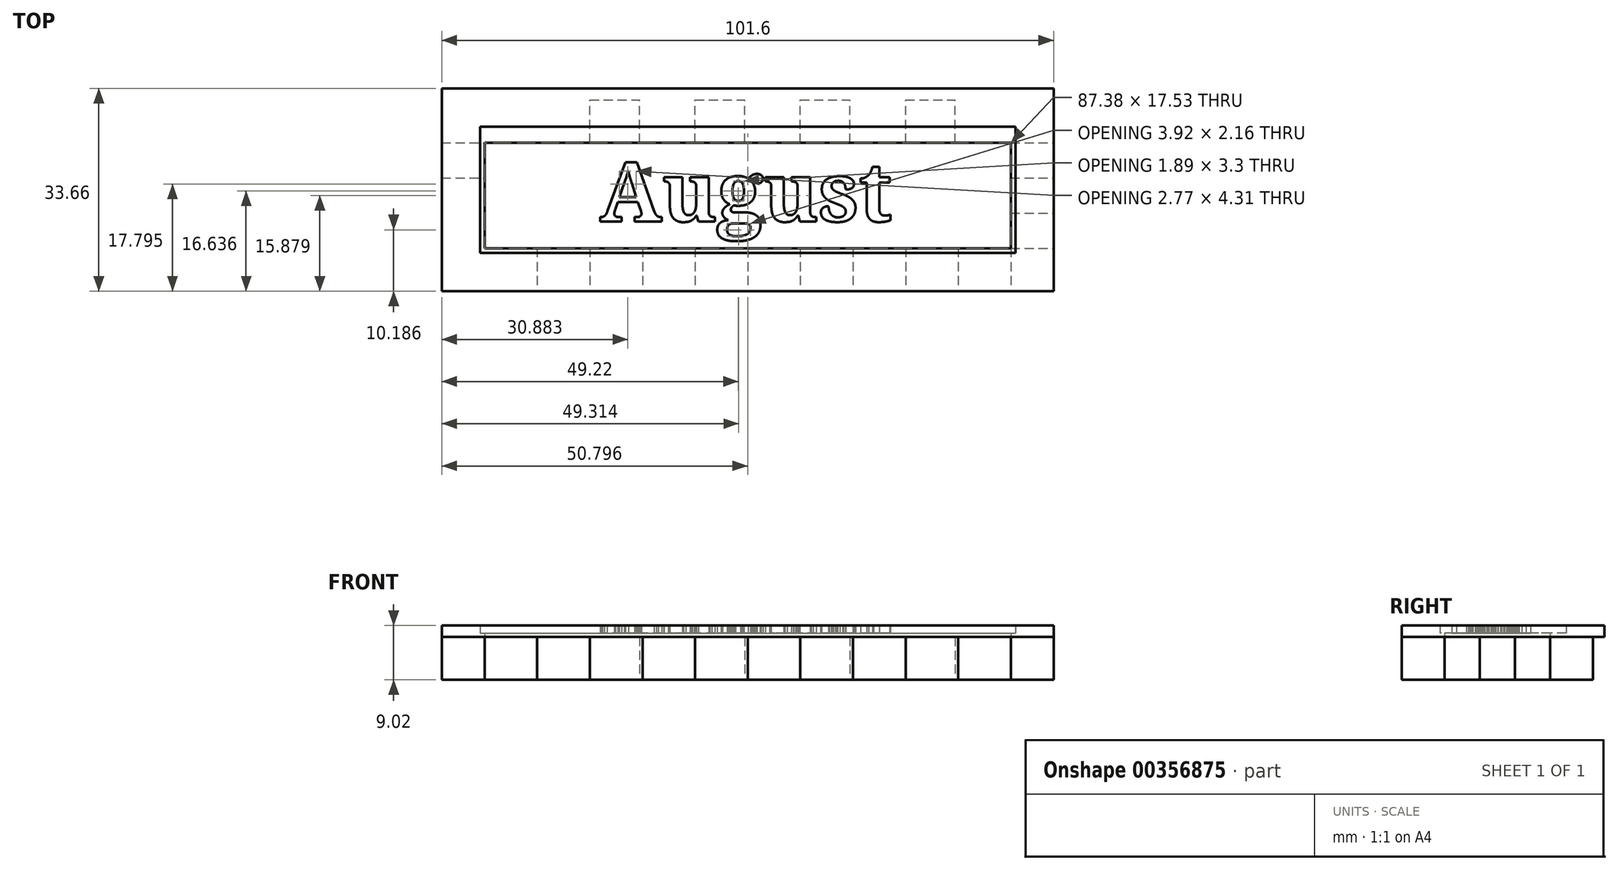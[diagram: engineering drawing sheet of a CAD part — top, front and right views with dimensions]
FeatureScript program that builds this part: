
annotation { "Feature Type Name" : "Feature", "Feature Type Description" : "" }
export const myFeature = defineFeature(function(context is Context, id is Id, definition is map)
    precondition{}
    {
        {
            var Q0;
            Q0=qCreatedBy(makeId("Top.planeOp"),FACE);
            var sketch = newSketch(context, id + "F0", { "sketchPlane" : qUnion([Q0])});
            skLineSegment(sketch, "E0.bottom", {"start": v(-52.12, 11.37) * mm, "end": v(49.48, 11.37) * mm});
            skLineSegment(sketch, "E0.top", {"start": v(-52.12, -20.38) * mm, "end": v(49.48, -20.38) * mm});
            skLineSegment(sketch, "E0.left", {"start": v(-52.12, 11.37) * mm, "end": v(-52.12, -20.38) * mm});
            skLineSegment(sketch, "E0.right", {"start": v(49.48, 11.37) * mm, "end": v(49.48, -20.38) * mm});
            skLineSegment(sketch, "E1.bottom", {"start": v(-52.12, 11.37) * mm, "end": v(-45.01, 11.37) * mm});
            skLineSegment(sketch, "E1.top", {"start": v(-52.12, 4.26) * mm, "end": v(-45.01, 4.26) * mm});
            skLineSegment(sketch, "E1.left", {"start": v(-52.12, 11.37) * mm, "end": v(-52.12, 4.26) * mm});
            skLineSegment(sketch, "E1.right", {"start": v(-45.01, 11.37) * mm, "end": v(-45.01, 4.26) * mm});
            skLineSegment(sketch, "E2.bottom", {"start": v(-45.01, 11.37) * mm, "end": v(-36.78, 11.37) * mm});
            skLineSegment(sketch, "E2.top", {"start": v(-45.01, 4.26) * mm, "end": v(-36.78, 4.26) * mm});
            skLineSegment(sketch, "E2.right", {"start": v(-36.78, 11.37) * mm, "end": v(-36.78, 4.26) * mm});
            skLineSegment(sketch, "E3.bottom", {"start": v(-36.78, 4.26) * mm, "end": v(-27.54, 4.26) * mm});
            skLineSegment(sketch, "E3.top", {"start": v(-36.78, 11.37) * mm, "end": v(-27.54, 11.37) * mm});
            skLineSegment(sketch, "E3.left", {"start": v(-36.78, 4.26) * mm, "end": v(-36.78, 11.37) * mm});
            skLineSegment(sketch, "E3.right", {"start": v(-27.54, 4.26) * mm, "end": v(-27.54, 11.37) * mm});
            skLineSegment(sketch, "E4.bottom", {"start": v(-27.54, 4.26) * mm, "end": v(-19.3, 4.26) * mm});
            skLineSegment(sketch, "E4.top", {"start": v(-27.54, 11.37) * mm, "end": v(-19.3, 11.37) * mm});
            skLineSegment(sketch, "E4.right", {"start": v(-19.3, 4.26) * mm, "end": v(-19.3, 11.37) * mm});
            skLineSegment(sketch, "E5.bottom", {"start": v(-19.3, 4.26) * mm, "end": v(-10.06, 4.26) * mm});
            skLineSegment(sketch, "E5.top", {"start": v(-19.3, 11.37) * mm, "end": v(-10.06, 11.37) * mm});
            skLineSegment(sketch, "E5.right", {"start": v(-10.06, 4.26) * mm, "end": v(-10.06, 11.37) * mm});
            skLineSegment(sketch, "E6.bottom", {"start": v(-10.06, 4.26) * mm, "end": v(-10.06, 4.26) * mm});
            skLineSegment(sketch, "E6.top", {"start": v(-10.06, 11.37) * mm, "end": v(-10.06, 11.37) * mm});
            skLineSegment(sketch, "E7.bottom", {"start": v(-10.06, 4.26) * mm, "end": v(-1.83, 4.26) * mm});
            skLineSegment(sketch, "E7.top", {"start": v(-10.06, 11.37) * mm, "end": v(-1.83, 11.37) * mm});
            skLineSegment(sketch, "E7.right", {"start": v(-1.83, 4.26) * mm, "end": v(-1.83, 11.37) * mm});
            skLineSegment(sketch, "E8.bottom", {"start": v(-1.83, 4.26) * mm, "end": v(7.41, 4.26) * mm});
            skLineSegment(sketch, "E8.top", {"start": v(-1.83, 11.37) * mm, "end": v(7.41, 11.37) * mm});
            skLineSegment(sketch, "E8.right", {"start": v(7.41, 4.26) * mm, "end": v(7.41, 11.37) * mm});
            skLineSegment(sketch, "E9.bottom", {"start": v(7.41, 4.26) * mm, "end": v(15.64, 4.26) * mm});
            skLineSegment(sketch, "E9.top", {"start": v(7.41, 11.37) * mm, "end": v(15.64, 11.37) * mm});
            skLineSegment(sketch, "E9.right", {"start": v(15.64, 4.26) * mm, "end": v(15.64, 11.37) * mm});
            skLineSegment(sketch, "E10.bottom", {"start": v(15.64, 4.26) * mm, "end": v(24.89, 4.26) * mm});
            skLineSegment(sketch, "E10.top", {"start": v(15.64, 11.37) * mm, "end": v(24.89, 11.37) * mm});
            skLineSegment(sketch, "E10.right", {"start": v(24.89, 4.26) * mm, "end": v(24.89, 11.37) * mm});
            skLineSegment(sketch, "E11.bottom", {"start": v(24.89, 4.26) * mm, "end": v(24.89, 4.26) * mm});
            skLineSegment(sketch, "E11.top", {"start": v(24.89, 11.37) * mm, "end": v(24.89, 11.37) * mm});
            skLineSegment(sketch, "E12.bottom", {"start": v(24.89, 4.26) * mm, "end": v(33.12, 4.26) * mm});
            skLineSegment(sketch, "E12.top", {"start": v(24.89, 11.37) * mm, "end": v(33.12, 11.37) * mm});
            skLineSegment(sketch, "E12.right", {"start": v(33.12, 4.26) * mm, "end": v(33.12, 11.37) * mm});
            skLineSegment(sketch, "E13.bottom", {"start": v(33.12, 4.26) * mm, "end": v(42.36, 4.26) * mm});
            skLineSegment(sketch, "E13.top", {"start": v(33.12, 11.37) * mm, "end": v(42.36, 11.37) * mm});
            skLineSegment(sketch, "E13.right", {"start": v(42.36, 4.26) * mm, "end": v(42.36, 11.37) * mm});
            skLineSegment(sketch, "E14.bottom", {"start": v(42.36, 4.26) * mm, "end": v(49.48, 4.26) * mm});
            skLineSegment(sketch, "E14.top", {"start": v(42.36, 11.37) * mm, "end": v(49.48, 11.37) * mm});
            skLineSegment(sketch, "E14.right", {"start": v(49.48, 4.26) * mm, "end": v(49.48, 11.37) * mm});
            skLineSegment(sketch, "E15.bottom", {"start": v(-52.12, -20.38) * mm, "end": v(-45.01, -20.38) * mm});
            skLineSegment(sketch, "E15.top", {"start": v(-52.12, -13.26) * mm, "end": v(-45.01, -13.26) * mm});
            skLineSegment(sketch, "E15.left", {"start": v(-52.12, -20.38) * mm, "end": v(-52.12, -13.26) * mm});
            skLineSegment(sketch, "E15.right", {"start": v(-45.01, -20.38) * mm, "end": v(-45.01, -13.26) * mm});
            skLineSegment(sketch, "E16.bottom", {"start": v(-45.01, -13.26) * mm, "end": v(-45.01, -13.26) * mm});
            skLineSegment(sketch, "E16.top", {"start": v(-45.01, -20.38) * mm, "end": v(-45.01, -20.38) * mm});
            skLineSegment(sketch, "E16.left", {"start": v(-45.01, -13.26) * mm, "end": v(-45.01, -20.38) * mm});
            skLineSegment(sketch, "E16.right", {"start": v(-45.01, -13.26) * mm, "end": v(-45.01, -20.38) * mm});
            skLineSegment(sketch, "E17.bottom", {"start": v(-45.01, -13.26) * mm, "end": v(-36.27, -13.26) * mm});
            skLineSegment(sketch, "E17.top", {"start": v(-45.01, -20.38) * mm, "end": v(-36.27, -20.38) * mm});
            skLineSegment(sketch, "E17.right", {"start": v(-36.27, -13.26) * mm, "end": v(-36.27, -20.38) * mm});
            skLineSegment(sketch, "E18.bottom", {"start": v(-36.27, -13.26) * mm, "end": v(-36.27, -13.26) * mm});
            skLineSegment(sketch, "E18.top", {"start": v(-36.27, -20.38) * mm, "end": v(-36.27, -20.38) * mm});
            skLineSegment(sketch, "E19.bottom", {"start": v(-36.27, -13.26) * mm, "end": v(-27.54, -13.26) * mm});
            skLineSegment(sketch, "E19.top", {"start": v(-36.27, -20.38) * mm, "end": v(-27.54, -20.38) * mm});
            skLineSegment(sketch, "E19.right", {"start": v(-27.54, -13.26) * mm, "end": v(-27.54, -20.38) * mm});
            skLineSegment(sketch, "E20.bottom", {"start": v(-27.54, -13.26) * mm, "end": v(-18.8, -13.26) * mm});
            skLineSegment(sketch, "E20.top", {"start": v(-27.54, -20.38) * mm, "end": v(-18.8, -20.38) * mm});
            skLineSegment(sketch, "E20.right", {"start": v(-18.8, -13.26) * mm, "end": v(-18.8, -20.38) * mm});
            skLineSegment(sketch, "E21.bottom", {"start": v(-18.8, -13.26) * mm, "end": v(-10.06, -13.26) * mm});
            skLineSegment(sketch, "E21.top", {"start": v(-18.8, -20.38) * mm, "end": v(-10.06, -20.38) * mm});
            skLineSegment(sketch, "E21.right", {"start": v(-10.06, -13.26) * mm, "end": v(-10.06, -20.38) * mm});
            skLineSegment(sketch, "E22.bottom", {"start": v(-10.06, -13.26) * mm, "end": v(-1.32, -13.26) * mm});
            skLineSegment(sketch, "E22.top", {"start": v(-10.06, -20.38) * mm, "end": v(-1.32, -20.38) * mm});
            skLineSegment(sketch, "E22.right", {"start": v(-1.32, -13.26) * mm, "end": v(-1.32, -20.38) * mm});
            skLineSegment(sketch, "E23.bottom", {"start": v(-1.32, -13.26) * mm, "end": v(7.41, -13.26) * mm});
            skLineSegment(sketch, "E23.top", {"start": v(-1.32, -20.38) * mm, "end": v(7.41, -20.38) * mm});
            skLineSegment(sketch, "E23.right", {"start": v(7.41, -13.26) * mm, "end": v(7.41, -20.38) * mm});
            skLineSegment(sketch, "E24.bottom", {"start": v(7.41, -13.26) * mm, "end": v(16.15, -13.26) * mm});
            skLineSegment(sketch, "E24.top", {"start": v(7.41, -20.38) * mm, "end": v(16.15, -20.38) * mm});
            skLineSegment(sketch, "E24.right", {"start": v(16.15, -13.26) * mm, "end": v(16.15, -20.38) * mm});
            skLineSegment(sketch, "E25.bottom", {"start": v(16.15, -13.26) * mm, "end": v(24.89, -13.26) * mm});
            skLineSegment(sketch, "E25.top", {"start": v(16.15, -20.38) * mm, "end": v(24.89, -20.38) * mm});
            skLineSegment(sketch, "E25.right", {"start": v(24.89, -13.26) * mm, "end": v(24.89, -20.38) * mm});
            skLineSegment(sketch, "E26.bottom", {"start": v(24.89, -13.26) * mm, "end": v(33.63, -13.26) * mm});
            skLineSegment(sketch, "E26.top", {"start": v(24.89, -20.38) * mm, "end": v(33.63, -20.38) * mm});
            skLineSegment(sketch, "E26.right", {"start": v(33.63, -13.26) * mm, "end": v(33.63, -20.38) * mm});
            skLineSegment(sketch, "E27.bottom", {"start": v(33.63, -13.26) * mm, "end": v(42.36, -13.26) * mm});
            skLineSegment(sketch, "E27.top", {"start": v(33.63, -20.38) * mm, "end": v(42.36, -20.38) * mm});
            skLineSegment(sketch, "E27.right", {"start": v(42.36, -13.26) * mm, "end": v(42.36, -20.38) * mm});
            skLineSegment(sketch, "E28.bottom", {"start": v(42.36, -13.26) * mm, "end": v(49.48, -13.26) * mm});
            skLineSegment(sketch, "E28.top", {"start": v(42.36, -20.38) * mm, "end": v(49.48, -20.38) * mm});
            skLineSegment(sketch, "E28.right", {"start": v(49.48, -13.26) * mm, "end": v(49.48, -20.38) * mm});
            skLineSegment(sketch, "E29.top", {"start": v(-52.12, -1.58) * mm, "end": v(-45.01, -1.58) * mm});
            skLineSegment(sketch, "E29.left", {"start": v(-52.12, 4.26) * mm, "end": v(-52.12, -1.58) * mm});
            skLineSegment(sketch, "E29.right", {"start": v(-45.01, 4.26) * mm, "end": v(-45.01, -1.58) * mm});
            skLineSegment(sketch, "E30.top", {"start": v(-52.12, -7.42) * mm, "end": v(-45.01, -7.42) * mm});
            skLineSegment(sketch, "E30.left", {"start": v(-52.12, -1.58) * mm, "end": v(-52.12, -7.42) * mm});
            skLineSegment(sketch, "E30.right", {"start": v(-45.01, -1.58) * mm, "end": v(-45.01, -7.42) * mm});
            skLineSegment(sketch, "E31.bottom", {"start": v(-45.01, -7.42) * mm, "end": v(-52.12, -7.42) * mm});
            skLineSegment(sketch, "E31.top", {"start": v(-45.01, -13.26) * mm, "end": v(-52.12, -13.26) * mm});
            skLineSegment(sketch, "E31.left", {"start": v(-45.01, -7.42) * mm, "end": v(-45.01, -13.26) * mm});
            skLineSegment(sketch, "E31.right", {"start": v(-52.12, -7.42) * mm, "end": v(-52.12, -13.26) * mm});
            skLineSegment(sketch, "E32.top", {"start": v(42.36, -1.58) * mm, "end": v(49.48, -1.58) * mm});
            skLineSegment(sketch, "E32.left", {"start": v(42.36, 4.26) * mm, "end": v(42.36, -1.58) * mm});
            skLineSegment(sketch, "E32.right", {"start": v(49.48, 4.26) * mm, "end": v(49.48, -1.58) * mm});
            skLineSegment(sketch, "E33.top", {"start": v(42.36, -7.42) * mm, "end": v(49.48, -7.42) * mm});
            skLineSegment(sketch, "E33.left", {"start": v(42.36, -1.58) * mm, "end": v(42.36, -7.42) * mm});
            skLineSegment(sketch, "E33.right", {"start": v(49.48, -1.58) * mm, "end": v(49.48, -7.42) * mm});
            skLineSegment(sketch, "E34.left", {"start": v(42.36, -7.42) * mm, "end": v(42.36, -13.26) * mm});
            skLineSegment(sketch, "E34.right", {"start": v(49.48, -7.42) * mm, "end": v(49.48, -13.26) * mm});
            skSolve(sketch);
        }
        {
            var Q0;
            Q0=makeQuery(id+"F0.imprint","IMPRINT",FACE,{"disambiguationData":[TD([[makeQuery(id+"F0.imprint","IMPRINT",EDGE,{"derivedFrom":sQuery(id+"F0.wireOp",EDGE,"E2.top")}),-1.0]])]});
            var Q1;
            Q1=makeQuery(id+"F0.imprint","IMPRINT",FACE,{"disambiguationData":[TD([[makeQuery(id+"F0.imprint","IMPRINT",EDGE,{"derivedFrom":sQuery(id+"F0.wireOp",EDGE,"E2.bottom")}),-1.0]])]});
            var Q2;
            Q2=makeQuery(id+"F0.imprint","IMPRINT",FACE,{"disambiguationData":[TD([[makeQuery(id+"F0.imprint","IMPRINT",EDGE,{"derivedFrom":sQuery(id+"F0.wireOp",EDGE,"E4.bottom")}),1.0]])]});
            var Q3;
            Q3=makeQuery(id+"F0.imprint","IMPRINT",FACE,{"disambiguationData":[TD([[makeQuery(id+"F0.imprint","IMPRINT",EDGE,{"derivedFrom":sQuery(id+"F0.wireOp",EDGE,"E7.bottom")}),1.0]])]});
            var Q4;
            Q4=makeQuery(id+"F0.imprint","IMPRINT",FACE,{"disambiguationData":[TD([[makeQuery(id+"F0.imprint","IMPRINT",EDGE,{"derivedFrom":sQuery(id+"F0.wireOp",EDGE,"E9.bottom")}),1.0]])]});
            var Q5;
            Q5=makeQuery(id+"F0.imprint","IMPRINT",FACE,{"disambiguationData":[TD([[makeQuery(id+"F0.imprint","IMPRINT",EDGE,{"derivedFrom":sQuery(id+"F0.wireOp",EDGE,"E12.bottom")}),1.0]])]});
            var Q6;
            Q6=makeQuery(id+"F0.imprint","IMPRINT",FACE,{"disambiguationData":[TD([[makeQuery(id+"F0.imprint","IMPRINT",EDGE,{"derivedFrom":sQuery(id+"F0.wireOp",EDGE,"E14.bottom")}),-1.0]])]});
            var Q7;
            Q7=makeQuery(id+"F0.imprint","IMPRINT",FACE,{"disambiguationData":[TD([[makeQuery(id+"F0.imprint","IMPRINT",EDGE,{"derivedFrom":sQuery(id+"F0.wireOp",EDGE,"E33.top")}),-1.0]])]});
            var Q8;
            Q8=makeQuery(id+"F0.imprint","IMPRINT",FACE,{"disambiguationData":[TD([[makeQuery(id+"F0.imprint","IMPRINT",EDGE,{"derivedFrom":sQuery(id+"F0.wireOp",EDGE,"E27.bottom")}),-1.0]])]});
            var Q9;
            Q9=makeQuery(id+"F0.imprint","IMPRINT",FACE,{"disambiguationData":[TD([[makeQuery(id+"F0.imprint","IMPRINT",EDGE,{"derivedFrom":sQuery(id+"F0.wireOp",EDGE,"E25.bottom")}),-1.0]])]});
            var Q10;
            Q10=makeQuery(id+"F0.imprint","IMPRINT",FACE,{"disambiguationData":[TD([[makeQuery(id+"F0.imprint","IMPRINT",EDGE,{"derivedFrom":sQuery(id+"F0.wireOp",EDGE,"E23.bottom")}),-1.0]])]});
            var Q11;
            Q11=makeQuery(id+"F0.imprint","IMPRINT",FACE,{"disambiguationData":[TD([[makeQuery(id+"F0.imprint","IMPRINT",EDGE,{"derivedFrom":sQuery(id+"F0.wireOp",EDGE,"E21.bottom")}),-1.0]])]});
            var Q12;
            Q12=makeQuery(id+"F0.imprint","IMPRINT",FACE,{"disambiguationData":[TD([[makeQuery(id+"F0.imprint","IMPRINT",EDGE,{"derivedFrom":sQuery(id+"F0.wireOp",EDGE,"E19.bottom")}),-1.0]])]});
            var Q13;
            Q13=makeQuery(id+"F0.imprint","IMPRINT",FACE,{"disambiguationData":[TD([[makeQuery(id+"F0.imprint","IMPRINT",EDGE,{"derivedFrom":sQuery(id+"F0.wireOp",EDGE,"E31.bottom")}),1.0]])]});
            var Q14;
            Q14=makeQuery(id+"F0.imprint","IMPRINT",FACE,{"disambiguationData":[TD([[makeQuery(id+"F0.imprint","IMPRINT",EDGE,{"derivedFrom":sQuery(id+"F0.wireOp",EDGE,"E1.top")}),-1.0]])]});
            extrude(context, id + "F1", {"entities" : qUnion([Q0, Q1, Q2, Q3, Q4, Q5, Q6, Q7, Q8, Q9, Q10, Q11, Q12, Q13, Q14]), "depth" : 7.11 * mm});
        }
        {
            var Q0;
            Q0=makeQuery(id+"F1.opExtrude","CAP_FACE",FACE,{"disambiguationData":[OSD([sQuery(id+"F0.wireOp",EDGE,"E2.bottom"),sQuery(id+"F0.wireOp",EDGE,"E1.right"),sQuery(id+"F0.wireOp",EDGE,"E3.bottom"),sQuery(id+"F0.wireOp",EDGE,"E3.left"),sQuery(id+"F0.wireOp",EDGE,"E4.top"),sQuery(id+"F0.wireOp",EDGE,"E3.right"),sQuery(id+"F0.wireOp",EDGE,"E5.bottom"),sQuery(id+"F0.wireOp",EDGE,"E4.right"),sQuery(id+"F0.wireOp",EDGE,"E6.top"),sQuery(id+"F0.wireOp",EDGE,"E5.right"),sQuery(id+"F0.wireOp",EDGE,"E7.bottom"),sQuery(id+"F0.wireOp",EDGE,"E5.right"),sQuery(id+"F0.wireOp",EDGE,"E8.top"),sQuery(id+"F0.wireOp",EDGE,"E7.right"),sQuery(id+"F0.wireOp",EDGE,"E9.bottom"),sQuery(id+"F0.wireOp",EDGE,"E8.right"),sQuery(id+"F0.wireOp",EDGE,"E10.top"),sQuery(id+"F0.wireOp",EDGE,"E9.right"),sQuery(id+"F0.wireOp",EDGE,"E11.bottom"),sQuery(id+"F0.wireOp",EDGE,"E10.right"),sQuery(id+"F0.wireOp",EDGE,"E12.top"),sQuery(id+"F0.wireOp",EDGE,"E10.right"),sQuery(id+"F0.wireOp",EDGE,"E13.bottom"),sQuery(id+"F0.wireOp",EDGE,"E12.right"),sQuery(id+"F0.wireOp",EDGE,"E16.bottom"),sQuery(id+"F0.wireOp",EDGE,"E17.top"),sQuery(id+"F0.wireOp",EDGE,"E16.left"),sQuery(id+"F0.wireOp",EDGE,"E18.bottom"),sQuery(id+"F0.wireOp",EDGE,"E17.right"),sQuery(id+"F0.wireOp",EDGE,"E19.top"),sQuery(id+"F0.wireOp",EDGE,"E17.right"),sQuery(id+"F0.wireOp",EDGE,"E20.bottom"),sQuery(id+"F0.wireOp",EDGE,"E19.right"),sQuery(id+"F0.wireOp",EDGE,"E21.top"),sQuery(id+"F0.wireOp",EDGE,"E20.right"),sQuery(id+"F0.wireOp",EDGE,"E22.bottom"),sQuery(id+"F0.wireOp",EDGE,"E21.right"),sQuery(id+"F0.wireOp",EDGE,"E23.top"),sQuery(id+"F0.wireOp",EDGE,"E22.right"),sQuery(id+"F0.wireOp",EDGE,"E24.bottom"),sQuery(id+"F0.wireOp",EDGE,"E23.right"),sQuery(id+"F0.wireOp",EDGE,"E25.top"),sQuery(id+"F0.wireOp",EDGE,"E24.right"),sQuery(id+"F0.wireOp",EDGE,"E26.bottom"),sQuery(id+"F0.wireOp",EDGE,"E25.right"),sQuery(id+"F0.wireOp",EDGE,"E27.top"),sQuery(id+"F0.wireOp",EDGE,"E26.right"),sQuery(id+"F0.wireOp",EDGE,"E27.right"),sQuery(id+"F0.wireOp",EDGE,"E1.top"),sQuery(id+"F0.wireOp",EDGE,"E29.left"),sQuery(id+"F0.wireOp",EDGE,"E29.top"),sQuery(id+"F0.wireOp",EDGE,"E30.right"),sQuery(id+"F0.wireOp",EDGE,"E31.bottom"),sQuery(id+"F0.wireOp",EDGE,"E31.top"),sQuery(id+"F0.wireOp",EDGE,"E31.right"),sQuery(id+"F0.wireOp",EDGE,"E14.bottom"),sQuery(id+"F0.wireOp",EDGE,"E32.right"),sQuery(id+"F0.wireOp",EDGE,"E32.top"),sQuery(id+"F0.wireOp",EDGE,"E33.left"),sQuery(id+"F0.wireOp",EDGE,"E33.top"),sQuery(id+"F0.wireOp",EDGE,"E28.bottom"),sQuery(id+"F0.wireOp",EDGE,"E34.right")])],"isStart":false});
            var sketch = newSketch(context, id + "F2", { "sketchPlane" : qUnion([Q0])});
            skLineSegment(sketch, "E35.bottom", {"start": v(-52.12, -20.38) * mm, "end": v(-45.01, -20.38) * mm});
            skLineSegment(sketch, "E35.top", {"start": v(-52.12, 13.28) * mm, "end": v(-45.01, 13.28) * mm});
            skLineSegment(sketch, "E35.left", {"start": v(-52.12, -20.38) * mm, "end": v(-52.12, 13.28) * mm});
            skLineSegment(sketch, "E35.right", {"start": v(-45.01, -20.38) * mm, "end": v(-45.01, 13.28) * mm});
            skLineSegment(sketch, "E36.bottom", {"start": v(-52.12, -20.38) * mm, "end": v(49.48, -20.38) * mm});
            skLineSegment(sketch, "E36.top", {"start": v(-52.12, -13.26) * mm, "end": v(49.48, -13.26) * mm});
            skLineSegment(sketch, "E36.left", {"start": v(-52.12, -20.38) * mm, "end": v(-52.12, -13.26) * mm});
            skLineSegment(sketch, "E36.right", {"start": v(49.48, -20.38) * mm, "end": v(49.48, -13.26) * mm});
            skPoint(sketch, "E37.oppositeSnap0", {"position": v(42.36, -4.5) * mm});
            skLineSegment(sketch, "E37.bottom", {"start": v(49.48, -20.38) * mm, "end": v(42.36, -20.38) * mm});
            skLineSegment(sketch, "E37.top", {"start": v(49.48, 13.28) * mm, "end": v(42.36, 13.28) * mm});
            skLineSegment(sketch, "E37.left", {"start": v(49.48, -20.38) * mm, "end": v(49.48, 13.28) * mm});
            skLineSegment(sketch, "E37.right", {"start": v(42.36, -20.38) * mm, "end": v(42.36, 13.28) * mm});
            skLineSegment(sketch, "E38.bottom", {"start": v(-52.12, 13.28) * mm, "end": v(49.48, 13.28) * mm});
            skLineSegment(sketch, "E38.top", {"start": v(-52.12, 4.26) * mm, "end": v(49.48, 4.26) * mm});
            skLineSegment(sketch, "E38.left", {"start": v(-52.12, 13.28) * mm, "end": v(-52.12, 4.26) * mm});
            skLineSegment(sketch, "E38.right", {"start": v(49.48, 13.28) * mm, "end": v(49.48, 4.26) * mm});
            skSolve(sketch);
        }
        {
            var Q0;
            Q0=qSketchRegion(id+"F2",true);
            var Q1;
            {var subQ5=sQuery(id+"F2.wireOp",EDGE,"E36.top");var subQ10=sQuery(id+"F2.wireOp",EDGE,"E35.right");var subQ12=makeQuery(id+"F2.imprint","INTERSECT",VERTEX,{"derivedFrom":[makeQuery(id+"F1.opExtrude","CAP_EDGE",EDGE,{"disambiguationData":[OSD([sQuery(id+"F0.wireOp",EDGE,"E31.bottom")])],"isStart":false}),subQ10]});var subQ24=makeQuery(id+"F2.imprint","INTERSECT",VERTEX,{"derivedFrom":[subQ10,subQ5]});Q1=makeQuery(id+"F2.imprint","IMPRINT",FACE,{"disambiguationData":[TD([[makeQuery(id+"F2.imprint","IMPRINT",EDGE,{"disambiguationData":[TD([[subQ12,1.0],[subQ24,-1.0]])],"derivedFrom":subQ10}),-1.0]])]});}
            extrude(context, id + "F3", {"entities" : qUnion([Q0, Q1]), "depth" : 0.64 * mm});
        }
        {
            var Q0;
            Q0=makeQuery(id+"F3.opExtrude","CAP_FACE",FACE,{"disambiguationData":[OSD([sQuery(id+"F2.wireOp",EDGE,"E35.left"),sQuery(id+"F2.wireOp",EDGE,"E36.bottom"),sQuery(id+"F2.wireOp",EDGE,"E36.left"),sQuery(id+"F2.wireOp",EDGE,"E37.bottom"),sQuery(id+"F2.wireOp",EDGE,"E37.left"),sQuery(id+"F2.wireOp",EDGE,"E38.bottom"),sQuery(id+"F2.wireOp",EDGE,"E38.left"),sQuery(id+"F2.wireOp",EDGE,"E38.right")])],"isStart":false});
            var sketch = newSketch(context, id + "F4", { "sketchPlane" : qUnion([Q0])});
            skLineSegment(sketch, "E39.bottom", {"start": v(-52.12, 13.28) * mm, "end": v(49.48, 13.28) * mm});
            skLineSegment(sketch, "E39.top", {"start": v(-52.12, 6.93) * mm, "end": v(49.48, 6.93) * mm});
            skLineSegment(sketch, "E39.left", {"start": v(-52.12, 13.28) * mm, "end": v(-52.12, 6.93) * mm});
            skLineSegment(sketch, "E39.right", {"start": v(49.48, 13.28) * mm, "end": v(49.48, 6.93) * mm});
            skLineSegment(sketch, "E40.bottom", {"start": v(-52.12, 13.28) * mm, "end": v(-45.77, 13.28) * mm});
            skLineSegment(sketch, "E40.top", {"start": v(-52.12, -20.38) * mm, "end": v(-45.77, -20.38) * mm});
            skLineSegment(sketch, "E40.left", {"start": v(-52.12, 13.28) * mm, "end": v(-52.12, -20.38) * mm});
            skLineSegment(sketch, "E40.right", {"start": v(-45.77, 13.28) * mm, "end": v(-45.77, -20.38) * mm});
            skLineSegment(sketch, "E41.bottom", {"start": v(-52.12, -14.03) * mm, "end": v(49.48, -14.03) * mm});
            skLineSegment(sketch, "E41.top", {"start": v(-52.12, -20.38) * mm, "end": v(49.48, -20.38) * mm});
            skLineSegment(sketch, "E41.left", {"start": v(-52.12, -14.03) * mm, "end": v(-52.12, -20.38) * mm});
            skLineSegment(sketch, "E41.right", {"start": v(49.48, -14.03) * mm, "end": v(49.48, -20.38) * mm});
            skLineSegment(sketch, "E42.bottom", {"start": v(49.48, -20.38) * mm, "end": v(43.13, -20.38) * mm});
            skLineSegment(sketch, "E42.top", {"start": v(49.48, 13.28) * mm, "end": v(43.13, 13.28) * mm});
            skLineSegment(sketch, "E42.left", {"start": v(49.48, -20.38) * mm, "end": v(49.48, 13.28) * mm});
            skLineSegment(sketch, "E42.right", {"start": v(43.13, -20.38) * mm, "end": v(43.13, 13.28) * mm});
            skSolve(sketch);
        }
        {
            var Q0;
            Q0=qSketchRegion(id+"F4",true);
            extrude(context, id + "F5", {"entities" : qUnion([Q0]), "operationType" : NewBodyOperationType.ADD, "depth" : 1.27 * mm});
        }
        {
            var Q0;
            Q0=makeQuery(id+"F3.opExtrude","CAP_FACE",FACE,{"disambiguationData":[OSD([sQuery(id+"F2.wireOp",EDGE,"E35.left"),sQuery(id+"F2.wireOp",EDGE,"E36.bottom"),sQuery(id+"F2.wireOp",EDGE,"E36.left"),sQuery(id+"F2.wireOp",EDGE,"E37.bottom"),sQuery(id+"F2.wireOp",EDGE,"E37.left"),sQuery(id+"F2.wireOp",EDGE,"E38.bottom"),sQuery(id+"F2.wireOp",EDGE,"E38.left"),sQuery(id+"F2.wireOp",EDGE,"E38.right")])],"isStart":false});
            var sketch = newSketch(context, id + "F6", { "sketchPlane" : qUnion([Q0])});
            skText(sketch, "E43", { "text": "August", "fontName": "NotoSerif-Bold.ttf"});
            const initialGuessF6  = {"E43": [-0.0259, -0.0088, 1, 0, 0.00988]};
            skSetInitialGuess(sketch, initialGuessF6);
            skSolve(sketch);
        }
        {
            var Q0;
            Q0 = qSketchRegion(id + "F6", true);
            extrude(context, id + "F7", {"entities" : qUnion([Q0]), "operationType" : NewBodyOperationType.ADD, "depth" : 1.27 * mm});
        }
    });
